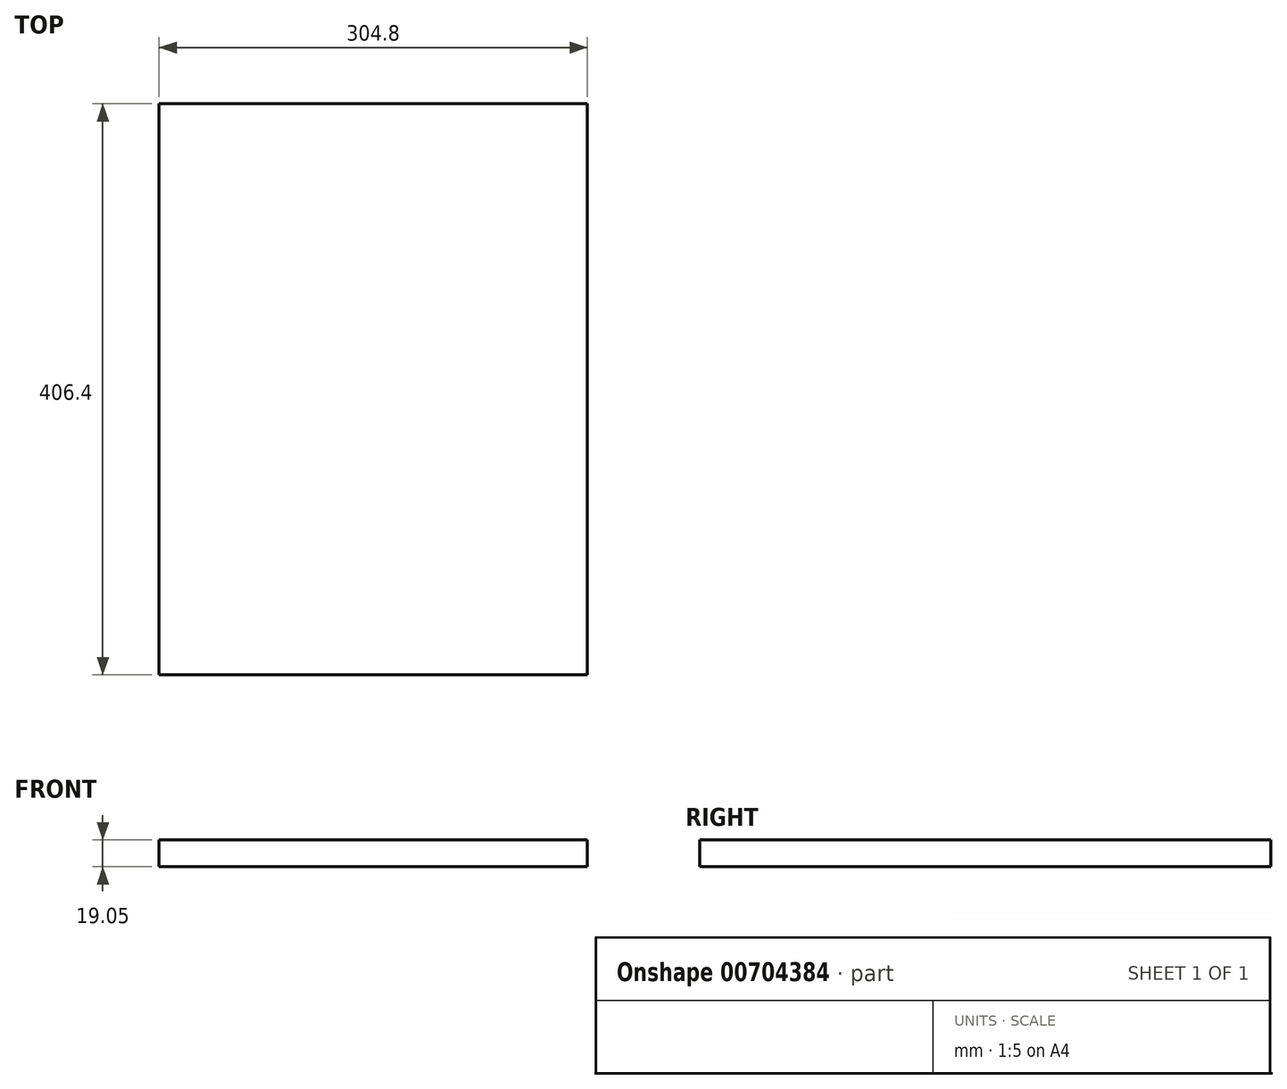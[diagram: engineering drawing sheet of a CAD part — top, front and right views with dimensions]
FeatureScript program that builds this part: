
annotation { "Feature Type Name" : "Feature", "Feature Type Description" : "" }
export const myFeature = defineFeature(function(context is Context, id is Id, definition is map)
    precondition{}
    {
        {
            var Q0;
            Q0=qCreatedBy(makeId("Top.planeOp"),FACE);
            var sketch = newSketch(context, id + "F0", { "sketchPlane" : qUnion([Q0])});
            skLineSegment(sketch, "E0.bottom", {"start": v(152.4, -203.2) * mm, "end": v(-152.4, -203.2) * mm});
            skLineSegment(sketch, "E0.top", {"start": v(152.4, 203.2) * mm, "end": v(-152.4, 203.2) * mm});
            skLineSegment(sketch, "E0.left", {"start": v(152.4, -203.2) * mm, "end": v(152.4, 203.2) * mm});
            skLineSegment(sketch, "E0.right", {"start": v(-152.4, -203.2) * mm, "end": v(-152.4, 203.2) * mm});
            skPoint(sketch, "E0.middle", {"position": v(0, 0) * mm});
            skSolve(sketch);
        }
        {
            var Q0;
            Q0 = qSketchRegion(id + "F0", true);
            extrude(context, id + "F1", {"entities" : qUnion([Q0]), "depth" : 19.05 * mm, "offsetDistance" : 25.4 * mm});
        }
    });
